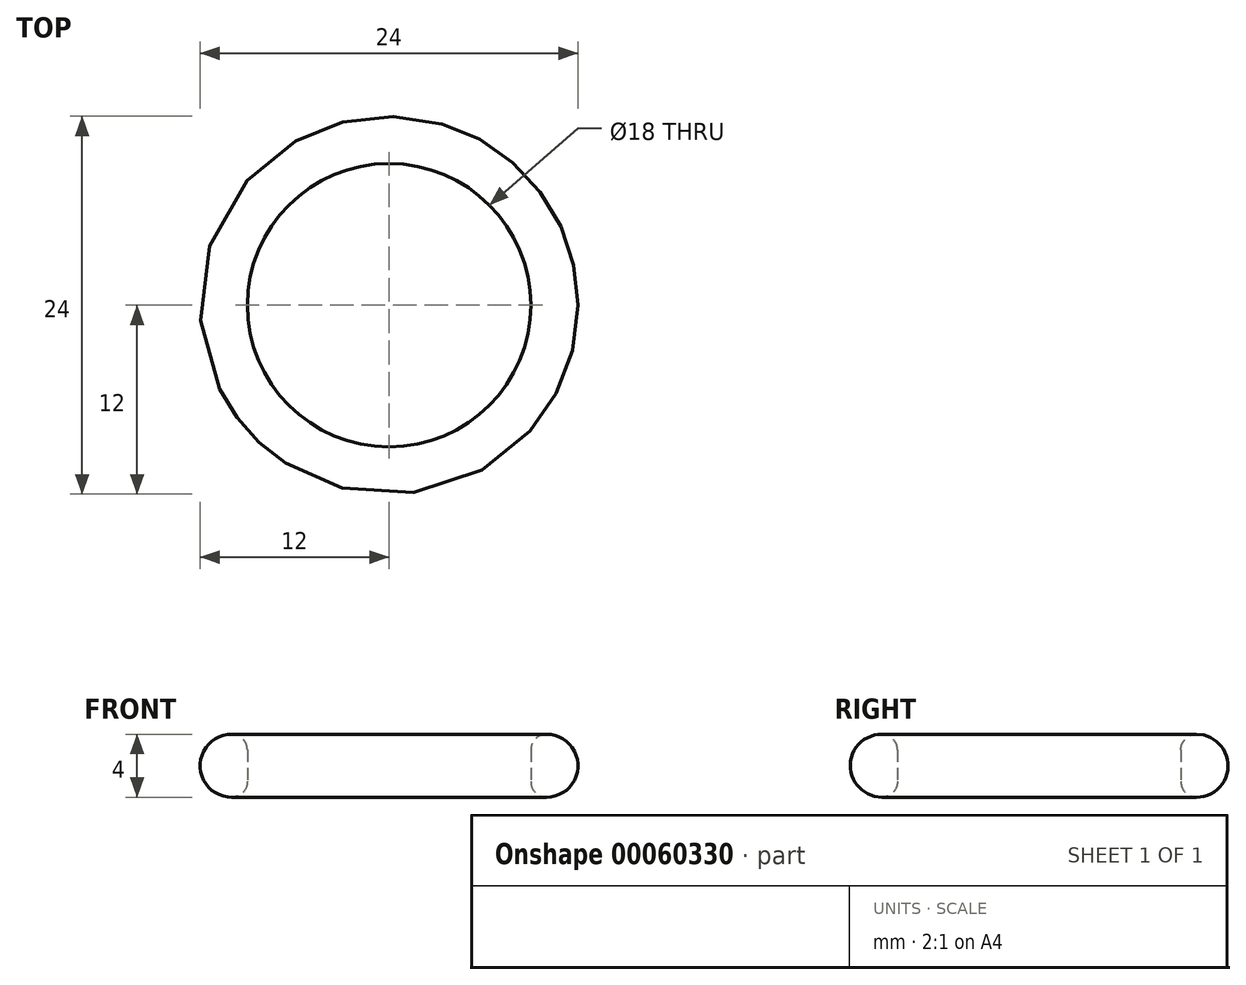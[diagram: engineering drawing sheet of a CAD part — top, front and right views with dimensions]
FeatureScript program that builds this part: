
annotation { "Feature Type Name" : "Feature", "Feature Type Description" : "" }
export const myFeature = defineFeature(function(context is Context, id is Id, definition is map)
    precondition{}
    {
        {
            var Q0;
            Q0=qCreatedBy(makeId("Right.planeOp"),FACE);
            var sketch = newSketch(context, id + "F0", { "sketchPlane" : qUnion([Q0])});
            skLineSegment(sketch, "E0.bottom", {"start": v(-12, 0) * mm, "end": v(-9, 0) * mm});
            skLineSegment(sketch, "E0.top", {"start": v(-12, 4) * mm, "end": v(-9, 4) * mm});
            skLineSegment(sketch, "E0.left", {"start": v(-12, 0) * mm, "end": v(-12, 4) * mm});
            skLineSegment(sketch, "E0.right", {"start": v(-9, 0) * mm, "end": v(-9, 4) * mm});
            skLineSegment(sketch, "E1", {"start": v(0, 0) * mm, "end": v(0, 5.05) * mm, "construction": true});
            skSolve(sketch);
        }
        {
            var Q0;
            Q0 = qSketchRegion(id + "F0", true);
            var Q1;
            Q1=sQuery(id+"F0.wireOp",EDGE,"E1");
            revolve(context, id + "F1", {"entities" : qUnion([Q0]), "axis" : qUnion([Q1]), "revolveType" : RevolveType.FULL});
        }
        {
            var Q0;
            Q0=makeQuery(id+"F1.opRevolve","SWEPT_EDGE",EDGE,{"disambiguationData":[OSD([sQuery(id+"F0.wireOp",EDGE,"E0.bottom"),sQuery(id+"F0.wireOp",EDGE,"E0.left")])]});
            var Q1;
            Q1=makeQuery(id+"F1.opRevolve","SWEPT_EDGE",EDGE,{"disambiguationData":[OSD([sQuery(id+"F0.wireOp",EDGE,"E0.top"),sQuery(id+"F0.wireOp",EDGE,"E0.left")])]});
            fillet(context, id + "F2", {"entities" : qUnion([Q0, Q1]), "radius" : 2 * mm, "allowEdgeOverflow" : false});
        }
        {
            var Q0;
            Q0=makeQuery(id+"F1.opRevolve","SWEPT_EDGE",EDGE,{"disambiguationData":[OSD([sQuery(id+"F0.wireOp",EDGE,"E0.bottom"),sQuery(id+"F0.wireOp",EDGE,"E0.right")])]});
            var Q1;
            Q1=makeQuery(id+"F1.opRevolve","SWEPT_EDGE",EDGE,{"disambiguationData":[OSD([sQuery(id+"F0.wireOp",EDGE,"E0.top"),sQuery(id+"F0.wireOp",EDGE,"E0.right")])]});
            fillet(context, id + "F3", {"entities" : qUnion([Q0, Q1]), "radius" : 1 * mm, "tangentPropagation" : true, "allowEdgeOverflow" : false});
        }
    });
